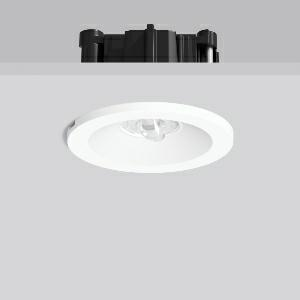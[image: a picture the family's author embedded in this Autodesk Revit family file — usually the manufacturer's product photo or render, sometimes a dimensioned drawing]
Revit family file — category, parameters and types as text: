
# Revit family: turia_l_672562_002_2508
name_source: partatom
category: Lighting Fixtures
units: mm (PartAtom-declared; Revit-internal decimal feet)

## family parameters
Cut with Voids When Loaded = No
Host = Face
Light Source = No
Part Type = Normal
Room Calculation Point = No
Round Connector Dimension = Use Diameter
Shared = No

## types (1)
- TURIA L (1 x LED Modul 765, 250 lm, 6500)
    Apparent Load = 4 VA
    CIE Flux Codes = 70 91 99 100 100
    Color Rendering = 70
    Color Temperature = 6500
    Default Elevation = 1800 mm
    Description = Series: TURIA L
Round emergency luminaire for escape route lighting. With asymmetrical beam plastic lenses for illuminating rescue facilities. Suitable for connection to central battery systems. With enclosed separate ceiling mounting ring also suitable for ceiling cut-outs of Ø 68 mm. 
Colour: white
Diameter: 62 mm
Height: 3 mm
Cut-out diameter: 54-68 mm
Recess height: 76-162 mm
Luminaire: recess height: 42 mm
Weight: 230 g
Operating mode: non-maintained power mode
Lamp: LED
Socket: without socket
Colour temperature: 6500K
Colour rendering index (CRI): 70
System power: 3.8 W
Rated luminous flux: 250 lm
Luminous flux, emergency: 250 lm
System power, emergency: 3.8 W
Control gear: Regulated power supply
Protection class: II
Type of protection: IP 20
    Height = 0 mm  [stored 0 ft]
    Lamp = 1 x LED Modul 765
    Lamp Light Flux = 250 lm
    Lamp count = 1
    Length = 62 mm  [stored 0.203412 ft]
    Lifetime = 50000 h
    Luminous efficacy = 66 lm/W
    Manufacturer = RZB
    ModVariant = No
    Model = 672562.002
    Mounting Place = Ceiling
    Mounting Type = Recessed
    Number of Poles = 1
    OnlyDefault = Yes
    Power Factor = 1
    Product Name = TURIA L
    Product group = Recessed ceiling luminaires
    ProductGroupID = 405
    Protection Class = Protection class II
    Protection Degree = IP 20
    RLX_Detail_Level = 1
    RLX_Emergency_Light_Flux = 250 lm
    RLX_Emergency_Type = 3
    RLX_Emergency_Type_DB = Yes
    RlxData = <blob elided: 55001 chars, md5=4c2ef5b9>
    Socket = socket
    Standby Power = 0 W
    System Light Flux = 250 lm
    System Power = 4 W
    Type Comments = Product without accessories
    Type Image = 672561.002.jpg
    URL = http://relux.com
    VarID = ---
    Voltage = 230 V
    Voltage Range = 220-240 V
    Weight = 0.00 kg
    Width = 0 mm  [stored 0 ft]

note: [stored X ft] marks values corroborated as IEEE doubles in the binary element streams (Revit-internal decimal feet)

## geometry (parser evidence)
native form markers: Blend x4, Sweep x10
no freeform markers — native parametric forms only
